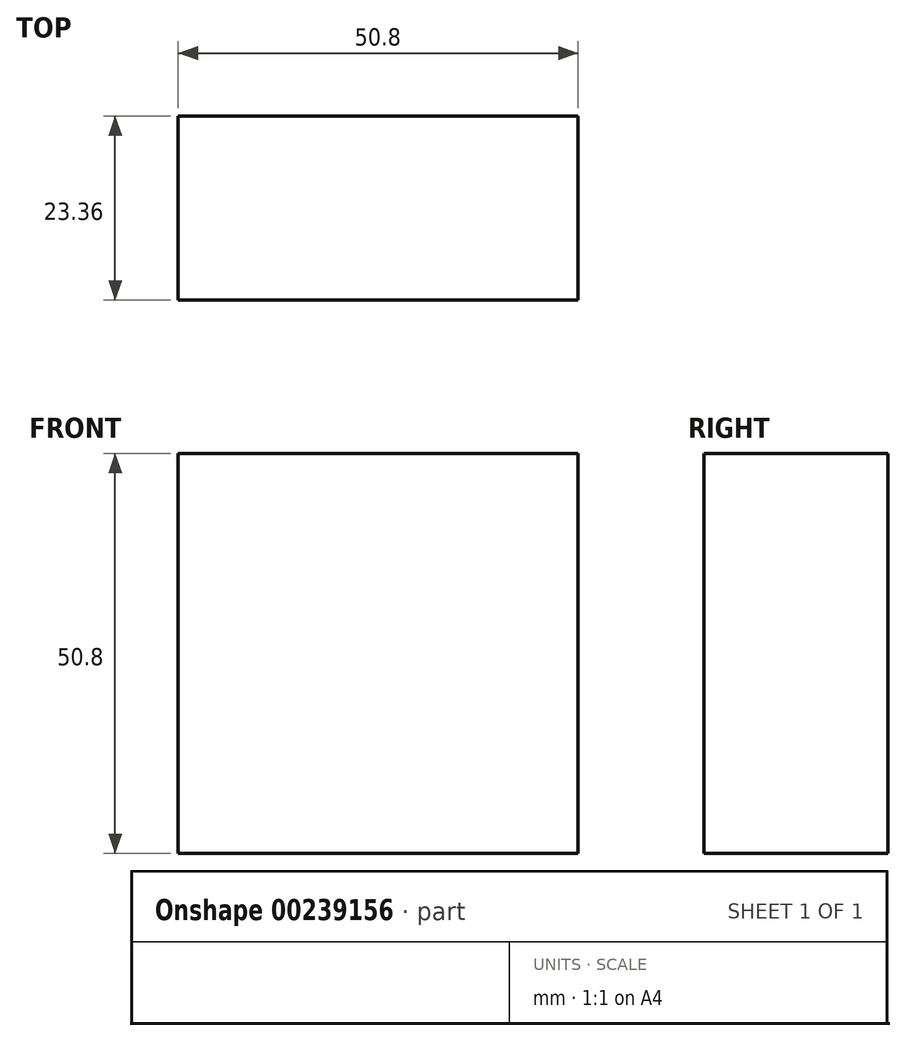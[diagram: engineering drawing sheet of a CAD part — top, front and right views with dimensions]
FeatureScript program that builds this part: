
annotation { "Feature Type Name" : "Feature", "Feature Type Description" : "" }
export const myFeature = defineFeature(function(context is Context, id is Id, definition is map)
    precondition{}
    {
        {
            var Q0;
            Q0=qCreatedBy(makeId("Front.planeOp"),FACE);
            var sketch = newSketch(context, id + "F0", { "sketchPlane" : qUnion([Q0])});
            skLineSegment(sketch, "E0.bottom", {"start": v(-23.88, 19.53) * mm, "end": v(26.92, 19.53) * mm});
            skLineSegment(sketch, "E0.top", {"start": v(-23.88, -31.27) * mm, "end": v(26.92, -31.27) * mm});
            skLineSegment(sketch, "E0.left", {"start": v(-23.88, 19.53) * mm, "end": v(-23.88, -31.27) * mm});
            skLineSegment(sketch, "E0.right", {"start": v(26.92, 19.53) * mm, "end": v(26.92, -31.27) * mm});
            skSolve(sketch);
        }
        {
            var Q0;
            Q0 = qSketchRegion(id + "F0", true);
            extrude(context, id + "F1", {"entities" : qUnion([Q0]), "endBound" : BoundingType.SYMMETRIC, "depth" : 23.37 * mm});
        }
    });
